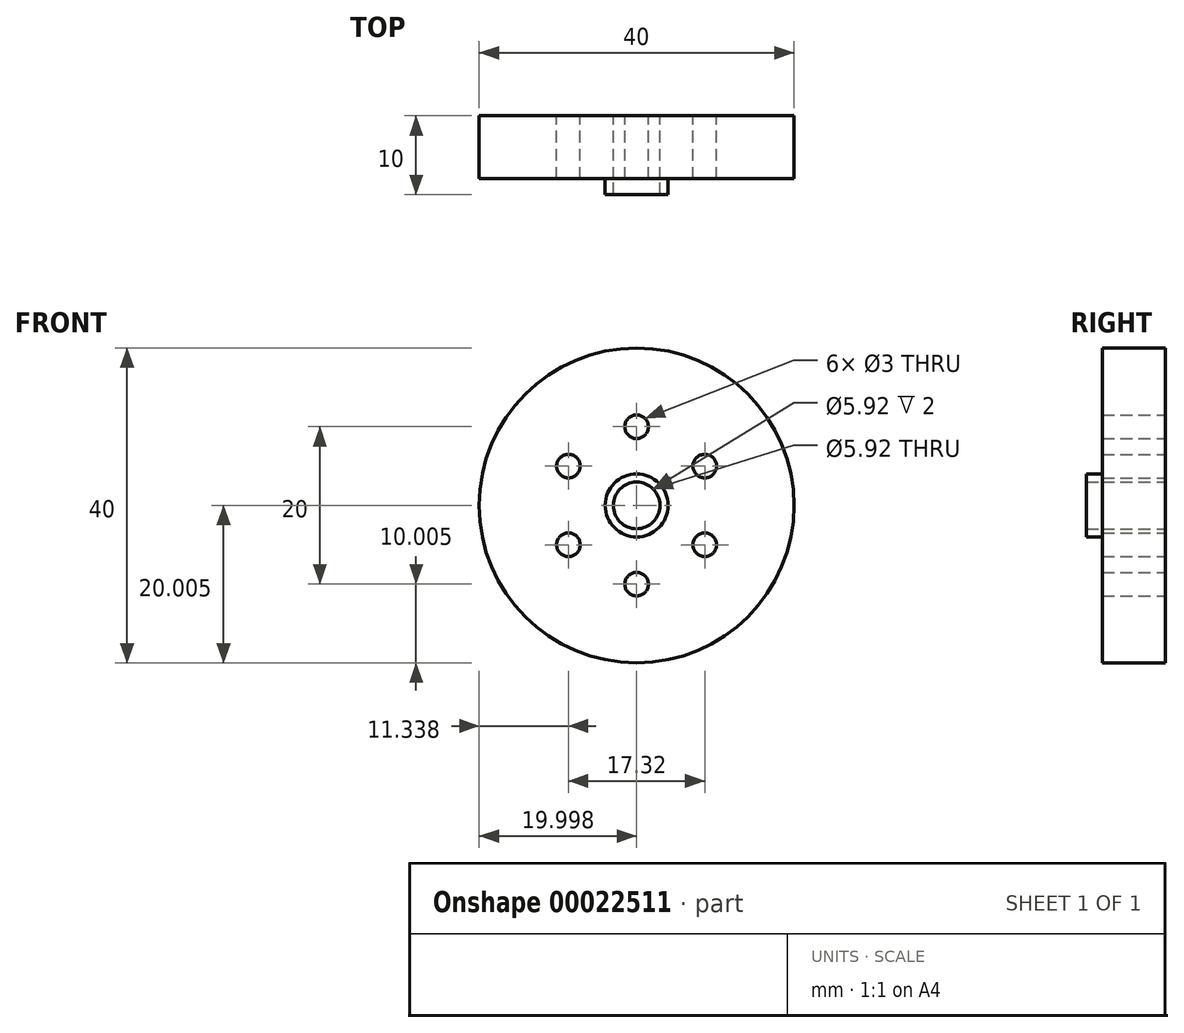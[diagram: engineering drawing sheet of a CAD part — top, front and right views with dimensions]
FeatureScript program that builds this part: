
annotation { "Feature Type Name" : "Feature", "Feature Type Description" : "" }
export const myFeature = defineFeature(function(context is Context, id is Id, definition is map)
    precondition{}
    {
        {
            var Q0;
            Q0=qCreatedBy(makeId("Front.planeOp"),FACE);
            var sketch = newSketch(context, id + "F0", { "sketchPlane" : qUnion([Q0])});
            skCircle(sketch, "E0", {"center": v(-32.3, 19.44) * mm, "radius": 20 * mm});
            skCircle(sketch, "E1", {"center": v(-32.3, 19.44) * mm, "radius": 2.5 * mm});
            skCircle(sketch, "E2", {"center": v(-32.3, 29.44) * mm, "radius": 1.5 * mm});
            skCircle(sketch, "E3.1.0", {"center": v(-40.96, 24.44) * mm, "radius": 1.5 * mm});
            skCircle(sketch, "E3.2.0", {"center": v(-40.96, 14.44) * mm, "radius": 1.5 * mm});
            skCircle(sketch, "E3.3.0", {"center": v(-32.3, 9.44) * mm, "radius": 1.5 * mm});
            skCircle(sketch, "E4.1.4.0", {"center": v(-23.64, 14.44) * mm, "radius": 1.5 * mm});
            skCircle(sketch, "E4.1.5.0", {"center": v(-23.64, 24.44) * mm, "radius": 1.5 * mm});
            skCircle(sketch, "E5", {"center": v(-32.3, 19.44) * mm, "radius": 2.96 * mm});
            skLineSegment(sketch, "E6", {"start": v(-52.3, 19.37) * mm, "end": v(-12.3, 19.37) * mm});
            skSolve(sketch);
        }
        {
            var Q0;
            Q0=qSketchRegion(id+"F0",true);
            extrude(context, id + "F1", {"entities" : qUnion([Q0]), "depth" : 3 * mm});
        }
        {
            var Q0;
            Q0=makeQuery(id+"F1.opExtrude","CAP_FACE",FACE,{"disambiguationData":[OSD([sQuery(id+"F0.wireOp",EDGE,"E0"),sQuery(id+"F0.wireOp",EDGE,"E1"),sQuery(id+"F0.wireOp",EDGE,"E2"),sQuery(id+"F0.wireOp",EDGE,"E3.1.0"),sQuery(id+"F0.wireOp",EDGE,"E3.2.0"),sQuery(id+"F0.wireOp",EDGE,"E3.3.0")])],"isStart":false});
            var sketch = newSketch(context, id + "F2", { "sketchPlane" : qUnion([Q0])});
            skCircle(sketch, "E7", {"center": v(-32.3, 19.44) * mm, "radius": 13 * mm});
            skSolve(sketch);
        }
        {
            var Q0;
            Q0=makeQuery(id+"F2.imprint","IMPRINT",FACE,{"disambiguationData":[TD([[makeQuery(id+"F2.imprint","IMPRINT",EDGE,{"derivedFrom":sQuery(id+"F2.wireOp",EDGE,"E7")}),1.0]])]});
            var Q1;
            Q1=makeQuery(id+"F2.imprint","IMPRINT",FACE,{"disambiguationData":[TD([[makeQuery(id+"F2.imprint","IMPRINT",EDGE,{"derivedFrom":sQuery(id+"F2.wireOp",EDGE,"E7")}),-1.0]])]});
            extrude(context, id + "F3", {"entities" : qUnion([Q0, Q1]), "operationType" : NewBodyOperationType.ADD, "depth" : 5 * mm});
        }
        {
            var Q0;
            Q0=makeQuery(id+"F3.opExtrude","CAP_FACE",FACE,{"disambiguationData":[OSD([sQuery(id+"F0.wireOp",EDGE,"E0"),sQuery(id+"F0.wireOp",EDGE,"E1"),sQuery(id+"F0.wireOp",EDGE,"E2"),sQuery(id+"F0.wireOp",EDGE,"E3.1.0"),sQuery(id+"F0.wireOp",EDGE,"E3.2.0"),sQuery(id+"F0.wireOp",EDGE,"E3.3.0")])],"isStart":false});
            var sketch = newSketch(context, id + "F4", { "sketchPlane" : qUnion([Q0])});
            skCircle(sketch, "E8", {"center": v(-32.3, 19.44) * mm, "radius": 4 * mm});
            skSolve(sketch);
        }
        {
            var Q0;
            Q0=makeQuery(id+"F4.imprint","IMPRINT",FACE,{"disambiguationData":[TD([[makeQuery(id+"F4.imprint","IMPRINT",EDGE,{"derivedFrom":sQuery(id+"F4.wireOp",EDGE,"E8")}),1.0]])]});
            extrude(context, id + "F5", {"entities" : qUnion([Q0]), "depth" : 2 * mm});
        }
    });
